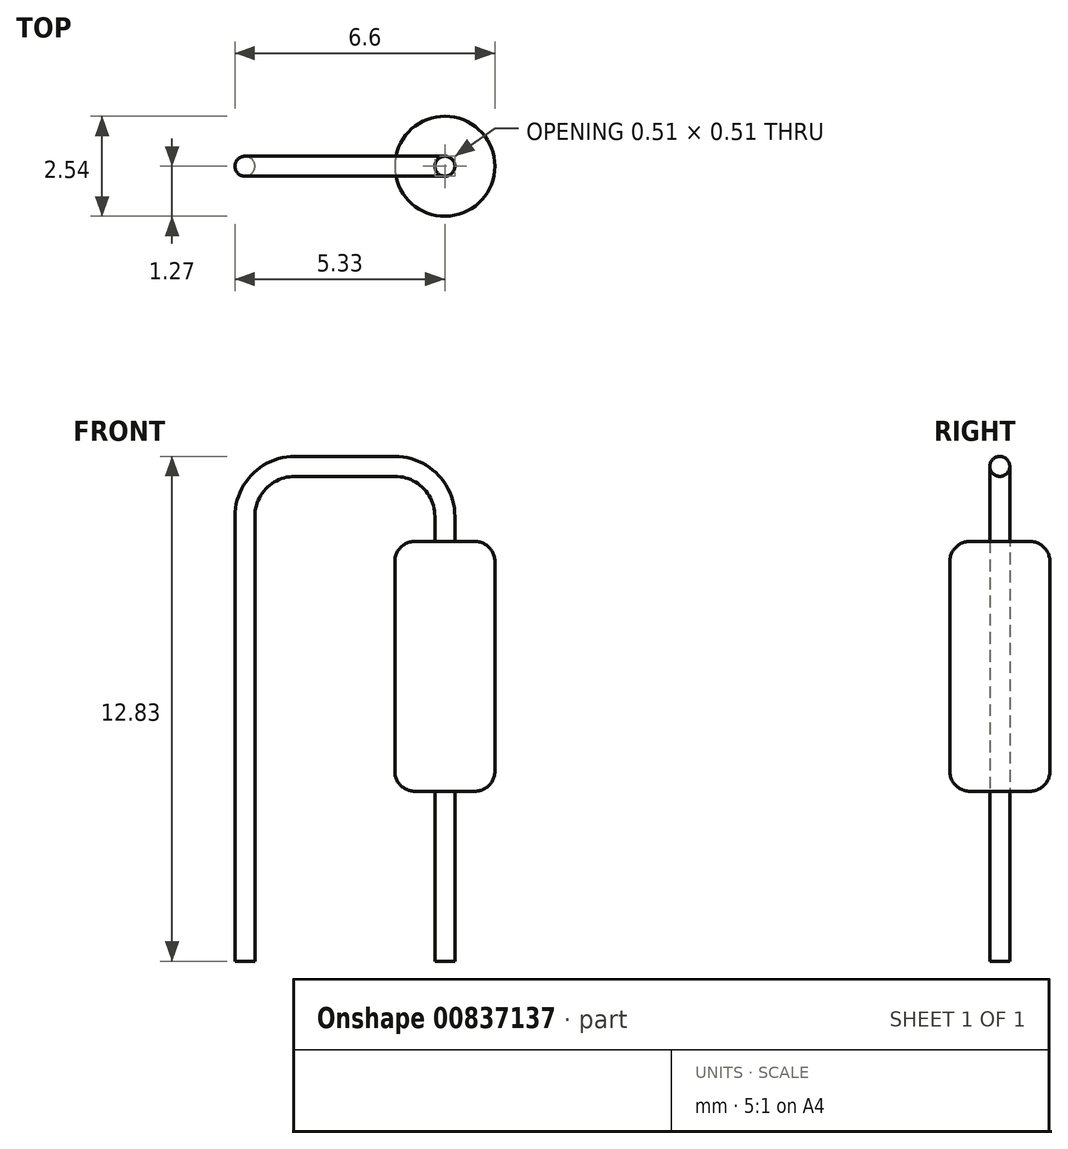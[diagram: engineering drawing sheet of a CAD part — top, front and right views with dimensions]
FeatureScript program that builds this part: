
annotation { "Feature Type Name" : "Feature", "Feature Type Description" : "" }
export const myFeature = defineFeature(function(context is Context, id is Id, definition is map)
    precondition{}
    {
        {
            var Q0;
            Q0=qCreatedBy(makeId("Front.planeOp"),FACE);
            var sketch = newSketch(context, id + "F0", { "sketchPlane" : qUnion([Q0])});
            skLineSegment(sketch, "E0.bottom", {"start": v(0, 0.5) * mm, "end": v(1.27, 0.5) * mm});
            skLineSegment(sketch, "E0.top", {"start": v(0, 6.86) * mm, "end": v(1.27, 6.86) * mm});
            skLineSegment(sketch, "E0.left", {"start": v(0, 0.5) * mm, "end": v(0, 6.86) * mm});
            skLineSegment(sketch, "E0.right", {"start": v(1.27, 0.5) * mm, "end": v(1.27, 6.86) * mm});
            skSolve(sketch);
        }
        {
            var Q0;
            Q0=qSketchRegion(id+"F0",true);
            var Q1;
            Q1=sQuery(id+"F0.wireOp",EDGE,"E0.left");
            revolve(context, id + "F1", {"surfaceOperationType" : NewSurfaceOperationType.NEW, "entities" : qUnion([Q0]), "axis" : qUnion([Q1]), "revolveType" : RevolveType.FULL});
        }
        {
            var Q0;
            Q0=makeQuery(id+"F1.opRevolve","SWEPT_EDGE",EDGE,{"disambiguationData":[OSD([sQuery(id+"F0.wireOp",EDGE,"E0.top"),sQuery(id+"F0.wireOp",EDGE,"E0.right")])]});
            var Q1;
            Q1=makeQuery(id+"F1.opRevolve","SWEPT_EDGE",EDGE,{"disambiguationData":[OSD([sQuery(id+"F0.wireOp",EDGE,"E0.bottom"),sQuery(id+"F0.wireOp",EDGE,"E0.right")])]});
            fillet(context, id + "F2", {"entities" : qUnion([Q0, Q1]), "radius" : 0.5 * mm, "tangentPropagation" : true, "allowEdgeOverflow" : false});
        }
        {
            var Q0;
            Q0=qCreatedBy(makeId("Front.planeOp"),FACE);
            var sketch = newSketch(context, id + "F3", { "sketchPlane" : qUnion([Q0])});
            skLineSegment(sketch, "E1", {"start": v(0, -3.81) * mm, "end": v(0, 7.5) * mm});
            skLineSegment(sketch, "E2", {"start": v(-5.08, 7.5) * mm, "end": v(-5.08, -3.81) * mm});
            skLineSegment(sketch, "E3", {"start": v(-5.08, -3.81) * mm, "end": v(0, -3.81) * mm, "construction": true});
            skLineSegment(sketch, "E4", {"start": v(0, 7.5) * mm, "end": v(-5.08, 7.5) * mm, "construction": true});
            skLineSegment(sketch, "E5", {"start": v(-3.81, 8.76) * mm, "end": v(-1.27, 8.76) * mm});
            skArc(sketch, "E6", {"start": v(0, 7.5) * mm, "mid": v(-0.37, 8.4) * mm, "end": v(-1.27, 8.76) * mm});
            skArc(sketch, "E7", {"start": v(-3.81, 8.76) * mm, "mid": v(-4.7, 8.4) * mm, "end": v(-5.08, 7.5) * mm});
            skSolve(sketch);
        }
        {
            var Q0;
            Q0=qCreatedBy(makeId("Top.planeOp"),FACE);
            cPlane(context, id + "F4", {"entities" : qUnion([Q0]), "cplaneType" : CPlaneType.OFFSET, "offset" : 3.8 * mm, "oppositeDirection" : true, "width" : 152.4 * mm, "height" : 152.4 * mm});
        }
        {
            var Q0;
            Q0=qCreatedBy(id+"F4.planeOp",FACE);
            var sketch = newSketch(context, id + "F5", { "sketchPlane" : qUnion([Q0])});
            skCircle(sketch, "E8", {"center": v(0, 0) * mm, "radius": 0.25 * mm});
            skSolve(sketch);
        }
        {
            var Q0;
            Q0=qSketchRegion(id+"F5",true);
            var Q1;
            Q1=qConstructionFilter(qBodyType(qCreatedBy(id+"F3",EDGE),BodyType.WIRE),ConstructionObject.NO);
            sweep(context, id + "F6", {"operationType" : NewBodyOperationType.ADD, "profiles" : qUnion([Q0]), "path" : qUnion([Q1])});
        }
    });
